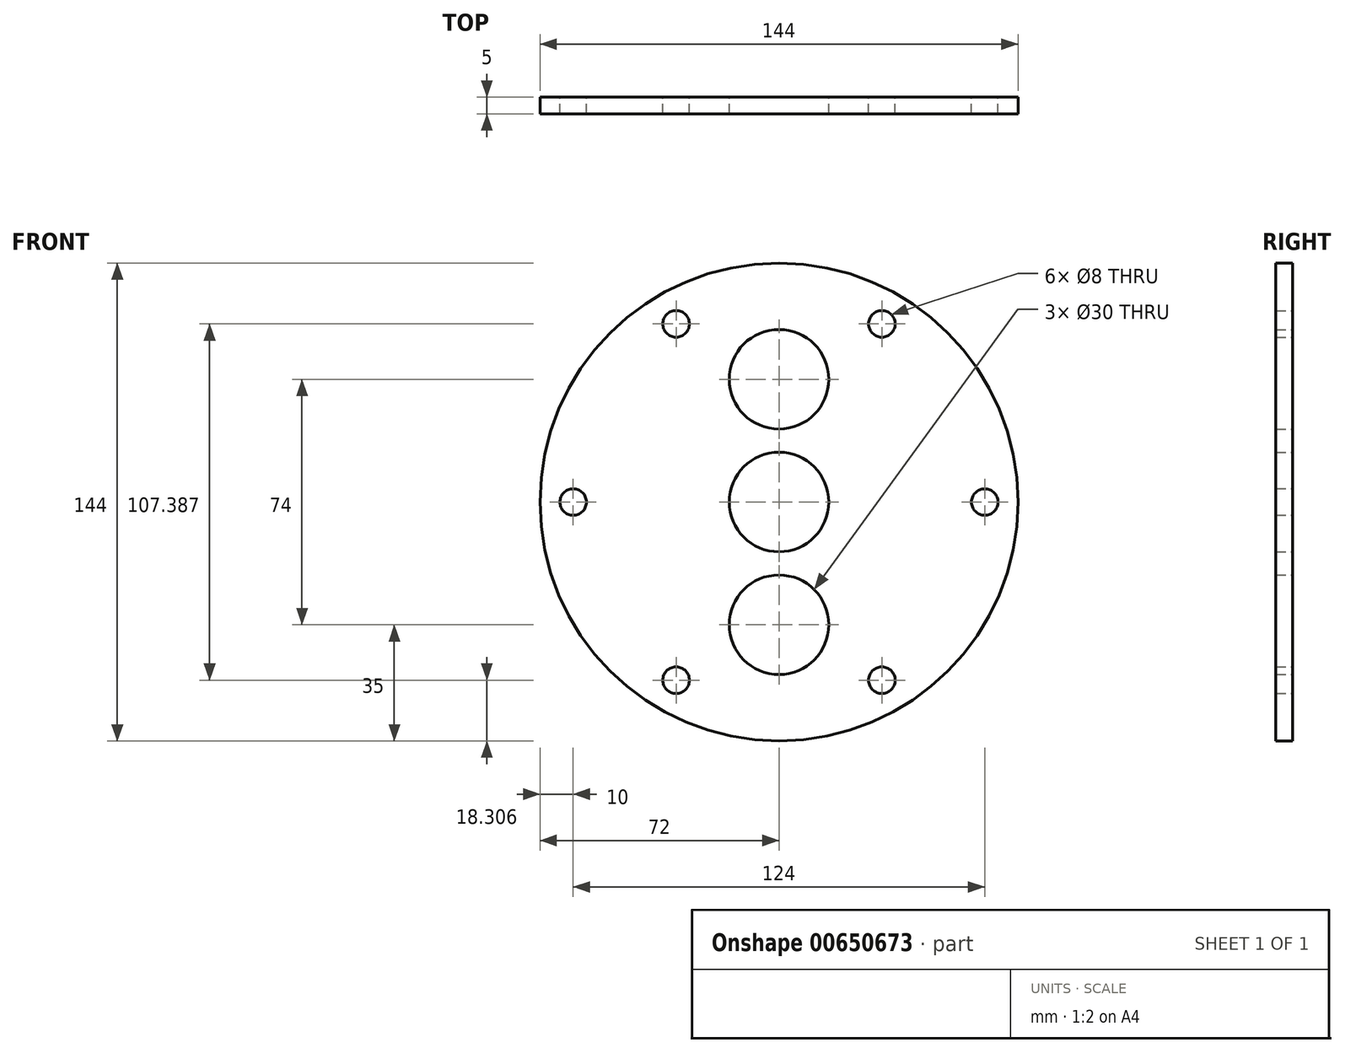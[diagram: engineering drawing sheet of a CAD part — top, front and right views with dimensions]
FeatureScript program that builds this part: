
annotation { "Feature Type Name" : "Feature", "Feature Type Description" : "" }
export const myFeature = defineFeature(function(context is Context, id is Id, definition is map)
    precondition{}
    {
        {
            var Q0;
            Q0=qCreatedBy(makeId("Front.planeOp"),FACE);
            var sketch = newSketch(context, id + "F0", { "sketchPlane" : qUnion([Q0])});
            skCircle(sketch, "E0", {"center": v(0, 0) * mm, "radius": 72 * mm});
            skCircle(sketch, "E1", {"center": v(0, 0) * mm, "radius": 62 * mm, "construction": true});
            skLineSegment(sketch, "E2", {"start": v(-43.78, 37) * mm, "end": v(39.74, 37) * mm, "construction": true});
            skLineSegment(sketch, "E3", {"start": v(39.74, -37) * mm, "end": v(-42.34, -37) * mm, "construction": true});
            skCircle(sketch, "E4", {"center": v(0, 37) * mm, "radius": 15 * mm});
            skCircle(sketch, "E5", {"center": v(0, 0) * mm, "radius": 15 * mm});
            skCircle(sketch, "E6", {"center": v(0, -37) * mm, "radius": 15 * mm});
            skPoint(sketch, "E6.centerSnap0", {"position": v(-1.3, -37) * mm});
            skCircle(sketch, "E7", {"center": v(62, 0) * mm, "radius": 4 * mm});
            skCircle(sketch, "E8.1.0", {"center": v(31, 53.7) * mm, "radius": 4 * mm});
            skCircle(sketch, "E8.2.0", {"center": v(-31, 53.7) * mm, "radius": 4 * mm});
            skCircle(sketch, "E8.3.0", {"center": v(-62, 0) * mm, "radius": 4 * mm});
            skCircle(sketch, "E8.4.0", {"center": v(-31, -53.7) * mm, "radius": 4 * mm});
            skCircle(sketch, "E8.5.0", {"center": v(31, -53.7) * mm, "radius": 4 * mm});
            skSolve(sketch);
        }
        {
            var Q0;
            Q0=makeQuery(id+"F0.imprint","IMPRINT",FACE,{"disambiguationData":[TD([[makeQuery(id+"F0.imprint","IMPRINT",EDGE,{"derivedFrom":sQuery(id+"F0.wireOp",EDGE,"E0")}),1.0]])]});
            extrude(context, id + "F1", {"entities" : qUnion([Q0]), "depth" : 5 * mm, "offsetDistance" : 25 * mm});
        }
    });
